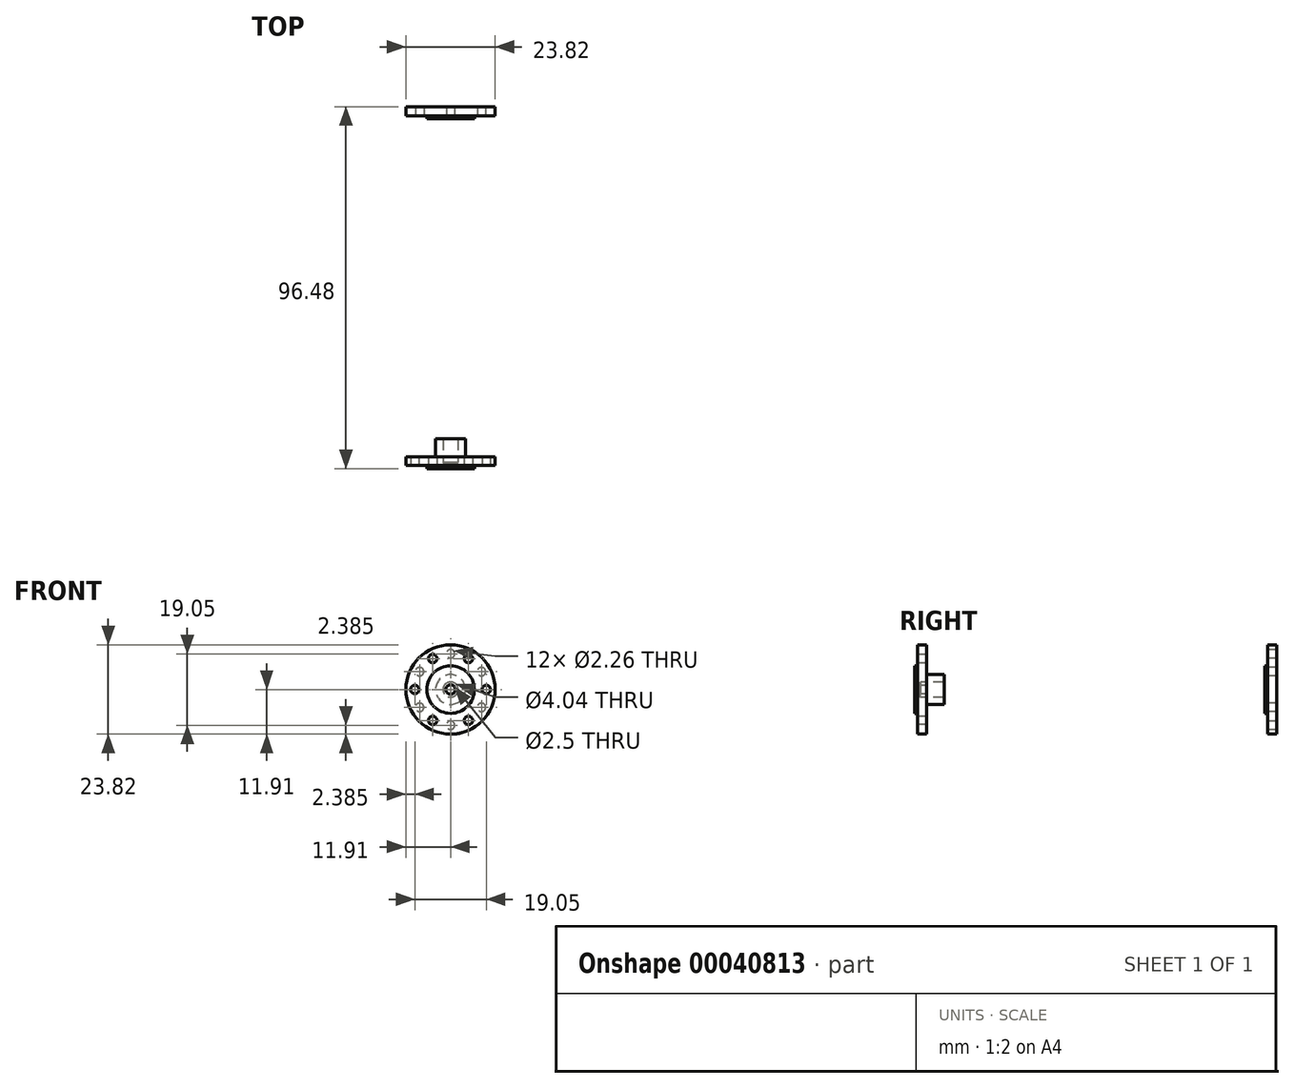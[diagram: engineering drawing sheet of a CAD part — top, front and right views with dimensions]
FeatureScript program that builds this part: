
annotation { "Feature Type Name" : "Feature", "Feature Type Description" : "" }
export const myFeature = defineFeature(function(context is Context, id is Id, definition is map)
    precondition{}
    {
        {
            var Q0;
            Q0=qCreatedBy(makeId("Front.planeOp"),FACE);
            var sketch = newSketch(context, id + "F0", { "sketchPlane" : qUnion([Q0])});
            skCircle(sketch, "E0", {"center": v(0, 0) * mm, "radius": 11.9 * mm});
            skPoint(sketch, "E1", {"position": v(0, 9.53) * mm});
            skPoint(sketch, "E2.1.0", {"position": v(-8.25, 4.76) * mm});
            skPoint(sketch, "E2.2.0", {"position": v(-8.25, -4.76) * mm});
            skPoint(sketch, "E2.3.0", {"position": v(0, -9.53) * mm});
            skPoint(sketch, "E2.4.0", {"position": v(8.25, -4.76) * mm});
            skPoint(sketch, "E2.5.0", {"position": v(8.25, 4.76) * mm});
            skCircle(sketch, "E3", {"center": v(0, 0) * mm, "radius": 6.35 * mm});
            skSolve(sketch);
        }
        {
            var Q0;
            Q0=makeQuery(id+"F0.imprint","IMPRINT",FACE,{"disambiguationData":[TD([[makeQuery(id+"F0.imprint","IMPRINT",EDGE,{"derivedFrom":sQuery(id+"F0.wireOp",EDGE,"E0")}),1.0]])]});
            extrude(context, id + "F1", {"entities" : qUnion([Q0]), "depth" : 2.38 * mm});
        }
        {
            var Q0;
            Q0=makeQuery(id+"F0.imprint","IMPRINT",FACE,{"disambiguationData":[TD([[makeQuery(id+"F0.imprint","IMPRINT",EDGE,{"derivedFrom":sQuery(id+"F0.wireOp",EDGE,"E3")}),1.0]])]});
            extrude(context, id + "F2", {"entities" : qUnion([Q0]), "operationType" : NewBodyOperationType.ADD, "depth" : 3.17 * mm});
        }
        {
            var Q0;
            Q0=sQuery(id+"F0.wireOp",VERTEX,"E1");
            var Q1;
            Q1=sQuery(id+"F0.wireOp",VERTEX,"E2.1.0");
            var Q2;
            Q2=sQuery(id+"F0.wireOp",VERTEX,"E2.2.0");
            var Q3;
            Q3=sQuery(id+"F0.wireOp",VERTEX,"E2.3.0");
            var Q4;
            Q4=sQuery(id+"F0.wireOp",VERTEX,"E2.4.0");
            var Q5;
            Q5=sQuery(id+"F0.wireOp",VERTEX,"E2.5.0");
            var Q6;
            Q6=makeQuery(id+"F1.opExtrude","SWEPT_BODY",BODY,{"disambiguationData":[OSD([sQuery(id+"F0.wireOp",EDGE,"E0"),sQuery(id+"F0.wireOp",EDGE,"E3")])]});
            hole(context, id + "F3", {"style" : HoleStyle.SIMPLE, "holeDiameter" : 2.26 * mm, "endStyle" : HoleEndStyle.THROUGH, "oppositeDirection" : true, "locations" : qUnion([Q0, Q1, Q2, Q3, Q4, Q5]), "scope" : qUnion([Q6])});
        }
        {
            var Q0;
            Q0=makeQuery(id+"F1.opExtrude","SWEPT_BODY",BODY,{"disambiguationData":[OSD([sQuery(id+"F0.wireOp",EDGE,"E0"),sQuery(id+"F0.wireOp",EDGE,"E3")])]});
            transform(context, id + "F4", {"entities" : qUnion([Q0]), "transformType" : TransformType.TRANSLATION_3D, "dx" : 0 * mm, "dy" : 93.3 * mm, "dz" : 0 * mm, "makeCopy" : false});
        }
        {
            var Q0;
            Q0=qCreatedBy(makeId("Front.planeOp"),FACE);
            var sketch = newSketch(context, id + "F5", { "sketchPlane" : qUnion([Q0])});
            skCircle(sketch, "E4", {"center": v(0, 0) * mm, "radius": 11.9 * mm});
            skCircle(sketch, "E5", {"center": v(0, 0) * mm, "radius": 6.35 * mm});
            skCircle(sketch, "E6", {"center": v(0, 0) * mm, "radius": 3.97 * mm});
            skPoint(sketch, "E7", {"position": v(0, 9.53) * mm});
            skPoint(sketch, "E8.1.0", {"position": v(-8.25, 4.76) * mm});
            skPoint(sketch, "E8.2.0", {"position": v(-8.25, -4.76) * mm});
            skPoint(sketch, "E8.3.0", {"position": v(0, -9.53) * mm});
            skPoint(sketch, "E8.4.0", {"position": v(8.25, -4.76) * mm});
            skPoint(sketch, "E8.5.0", {"position": v(8.25, 4.76) * mm});
            skSolve(sketch);
        }
        {
            var Q0;
            Q0=makeQuery(id+"F5.imprint","IMPRINT",FACE,{"disambiguationData":[TD([[makeQuery(id+"F5.imprint","IMPRINT",EDGE,{"derivedFrom":sQuery(id+"F5.wireOp",EDGE,"E4")}),1.0]])]});
            extrude(context, id + "F6", {"entities" : qUnion([Q0]), "depth" : 2.38 * mm});
        }
        {
            var Q0;
            Q0=makeQuery(id+"F5.imprint","IMPRINT",FACE,{"disambiguationData":[TD([[makeQuery(id+"F5.imprint","IMPRINT",EDGE,{"derivedFrom":sQuery(id+"F5.wireOp",EDGE,"E5")}),1.0]])]});
            var Q1;
            Q1=sQuery(id+"F5.wireOp",EDGE,"E5");
            extrude(context, id + "F7", {"entities" : qUnion([Q0]), "operationType" : NewBodyOperationType.ADD, "surfaceEntities" : qUnion([Q1]), "depth" : 3.17 * mm});
        }
        {
            var Q0;
            Q0=makeQuery(id+"F5.imprint","IMPRINT",FACE,{"disambiguationData":[TD([[makeQuery(id+"F5.imprint","IMPRINT",EDGE,{"derivedFrom":sQuery(id+"F5.wireOp",EDGE,"E6")}),1.0]])]});
            extrude(context, id + "F8", {"entities" : qUnion([Q0]), "operationType" : NewBodyOperationType.ADD, "oppositeDirection" : true, "depth" : 4.76 * mm, "hasSecondDirection" : true, "secondDirectionOppositeDirection" : false, "secondDirectionDepth" : 3.17 * mm});
        }
        {
            var Q0;
            Q0=sQuery(id+"F5.wireOp",VERTEX,"E7");
            var Q1;
            Q1=sQuery(id+"F5.wireOp",VERTEX,"E8.1.0");
            var Q2;
            Q2=sQuery(id+"F5.wireOp",VERTEX,"E8.2.0");
            var Q3;
            Q3=sQuery(id+"F5.wireOp",VERTEX,"E8.3.0");
            var Q4;
            Q4=sQuery(id+"F5.wireOp",VERTEX,"E8.4.0");
            var Q5;
            Q5=sQuery(id+"F5.wireOp",VERTEX,"E8.5.0");
            var Q6;
            Q6=makeQuery(id+"F6.opExtrude","SWEPT_BODY",BODY,{"disambiguationData":[OSD([sQuery(id+"F5.wireOp",EDGE,"E4"),sQuery(id+"F5.wireOp",EDGE,"E5")])]});
            hole(context, id + "F9", {"style" : HoleStyle.SIMPLE, "holeDiameter" : 2.26 * mm, "endStyle" : HoleEndStyle.THROUGH, "oppositeDirection" : true, "locations" : qUnion([Q0, Q1, Q2, Q3, Q4, Q5]), "scope" : qUnion([Q6])});
        }
        {
            var Q0;
            Q0=makeQuery(id+"F8.opExtrude","CAP_FACE",FACE,{"disambiguationData":[OSD([sQuery(id+"F5.wireOp",EDGE,"E6")])],"isStart":false});
            var sketch = newSketch(context, id + "F10", { "sketchPlane" : qUnion([Q0])});
            skPoint(sketch, "E9", {"position": v(0, 0) * mm});
            skCircle(sketch, "E10", {"center": v(0, 0) * mm, "radius": 1.25 * mm});
            skSolve(sketch);
        }
        {
            var Q0;
            Q0=sQuery(id+"F10.wireOp",VERTEX,"E9");
            var Q1;
            Q1=makeQuery(id+"F6.opExtrude","SWEPT_BODY",BODY,{"disambiguationData":[OSD([sQuery(id+"F5.wireOp",EDGE,"E4"),sQuery(id+"F5.wireOp",EDGE,"E5")])]});
            hole(context, id + "F11", {"style" : HoleStyle.SIMPLE, "holeDiameter" : 4.04 * mm, "endStyle" : HoleEndStyle.BLIND, "holeDepth" : 6.35 * mm, "locations" : qUnion([Q0]), "scope" : qUnion([Q1])});
        }
        {
            var Q0;
            Q0=makeQuery(id+"F10.imprint","IMPRINT",FACE,{"disambiguationData":[TD([[makeQuery(id+"F10.imprint","IMPRINT",EDGE,{"derivedFrom":sQuery(id+"F10.wireOp",EDGE,"E10")}),1.0]])]});
            var Q1;
            Q1=sQuery(id+"F10.wireOp",EDGE,"E10");
            extrude(context, id + "F12", {"entities" : qUnion([Q0]), "operationType" : NewBodyOperationType.REMOVE, "surfaceEntities" : qUnion([Q1]), "endBound" : BoundingType.THROUGH_ALL, "oppositeDirection" : true, "depth" : 25.4 * mm});
        }
        {
            var Q0;
            Q0=makeQuery(id+"F6.opExtrude","SWEPT_BODY",BODY,{"disambiguationData":[OSD([sQuery(id+"F5.wireOp",EDGE,"E4"),sQuery(id+"F5.wireOp",EDGE,"E5")])]});
            var Q1;
            Q1=makeQuery(id+"F8.opExtrude","SWEPT_FACE",FACE,{"disambiguationData":[OSD([sQuery(id+"F5.wireOp",EDGE,"E6")])]});
            transform(context, id + "F13", {"entities" : qUnion([Q0]), "transformType" : TransformType.ROTATION, "transformAxis" : qUnion([Q1]), "angle" : 30 * degree, "makeCopy" : false});
        }
    });
